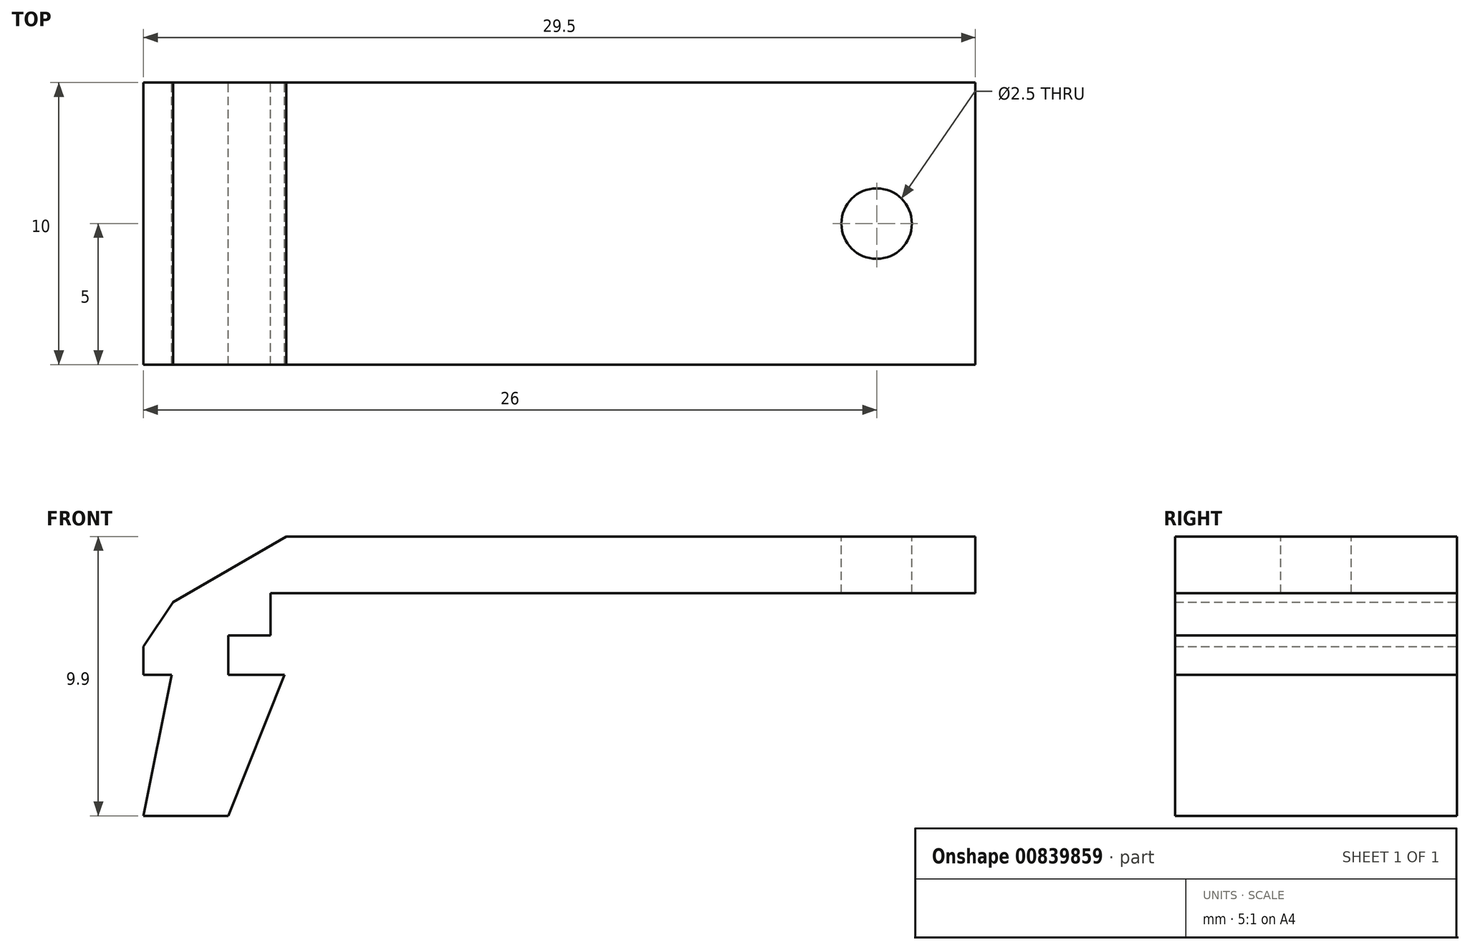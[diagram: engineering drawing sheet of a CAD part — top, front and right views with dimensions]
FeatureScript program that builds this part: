
annotation { "Feature Type Name" : "Feature", "Feature Type Description" : "" }
export const myFeature = defineFeature(function(context is Context, id is Id, definition is map)
    precondition{}
    {
        {
            var Q0;
            Q0=qCreatedBy(makeId("Front.planeOp"),FACE);
            var sketch = newSketch(context, id + "F0", { "sketchPlane" : qUnion([Q0])});
            skLineSegment(sketch, "E0", {"start": v(0, 0) * mm, "end": v(0, 0) * mm});
            skLineSegment(sketch, "E1", {"start": v(0, 0) * mm, "end": v(2, 5) * mm});
            skLineSegment(sketch, "E2", {"start": v(2, 5) * mm, "end": v(0, 5) * mm});
            skLineSegment(sketch, "E3", {"start": v(0, 5) * mm, "end": v(0, 6.4) * mm});
            skLineSegment(sketch, "E4", {"start": v(-3, 5) * mm, "end": v(-2, 5) * mm});
            skLineSegment(sketch, "E5", {"start": v(-2, 5) * mm, "end": v(-3, 0) * mm});
            skLineSegment(sketch, "E6", {"start": v(-3, 0) * mm, "end": v(0, 0) * mm});
            skLineSegment(sketch, "E7", {"start": v(0, 5) * mm, "end": v(0, 0) * mm, "construction": true});
            skLineSegment(sketch, "E8", {"start": v(0, 6.4) * mm, "end": v(1.5, 6.4) * mm});
            skLineSegment(sketch, "E9", {"start": v(1.5, 6.4) * mm, "end": v(1.5, 7.9) * mm});
            skLineSegment(sketch, "E10", {"start": v(1.5, 7.9) * mm, "end": v(26.5, 7.9) * mm});
            skLineSegment(sketch, "E11", {"start": v(26.5, 7.9) * mm, "end": v(26.5, 9.9) * mm});
            skLineSegment(sketch, "E12", {"start": v(26.5, 9.9) * mm, "end": v(-3, 9.9) * mm});
            skLineSegment(sketch, "E13", {"start": v(-3, 9.9) * mm, "end": v(-3, 5) * mm});
            skLineSegment(sketch, "E14", {"start": v(-3, 6.98) * mm, "end": v(2.06, 9.9) * mm});
            skLineSegment(sketch, "E15", {"start": v(-3, 6) * mm, "end": v(-1.96, 7.58) * mm});
            skSolve(sketch);
        }
        {
            var Q0;
            Q0=makeQuery(id+"F0.imprint","IMPRINT",FACE,{"disambiguationData":[TD([[makeQuery(id+"F0.imprint","IMPRINT",EDGE,{"derivedFrom":sQuery(id+"F0.wireOp",EDGE,"E1")}),1.0]])]});
            extrude(context, id + "F1", {"entities" : qUnion([Q0]), "depth" : 10 * mm, "offsetDistance" : 25 * mm});
        }
        {
            var Q0;
            Q0=makeQuery(id+"F1.opExtrude","SWEPT_FACE",FACE,{"disambiguationData":[OSD([sQuery(id+"F0.wireOp",EDGE,"E12")])]});
            var sketch = newSketch(context, id + "F2", { "sketchPlane" : qUnion([Q0])});
            skCircle(sketch, "E16", {"center": v(23, -5) * mm, "radius": 1.25 * mm});
            skLineSegment(sketch, "E17", {"start": v(21.75, 0) * mm, "end": v(21.75, -8.88) * mm, "construction": true});
            skSolve(sketch);
        }
        {
            var Q0;
            Q0=makeQuery(id+"F2.imprint","IMPRINT",FACE,{"disambiguationData":[TD([[makeQuery(id+"F2.imprint","IMPRINT",EDGE,{"derivedFrom":sQuery(id+"F2.wireOp",EDGE,"E16")}),1.0]])]});
            extrude(context, id + "F3", {"entities" : qUnion([Q0]), "operationType" : NewBodyOperationType.REMOVE, "oppositeDirection" : true, "depth" : 25 * mm, "offsetDistance" : 25 * mm});
        }
    });
